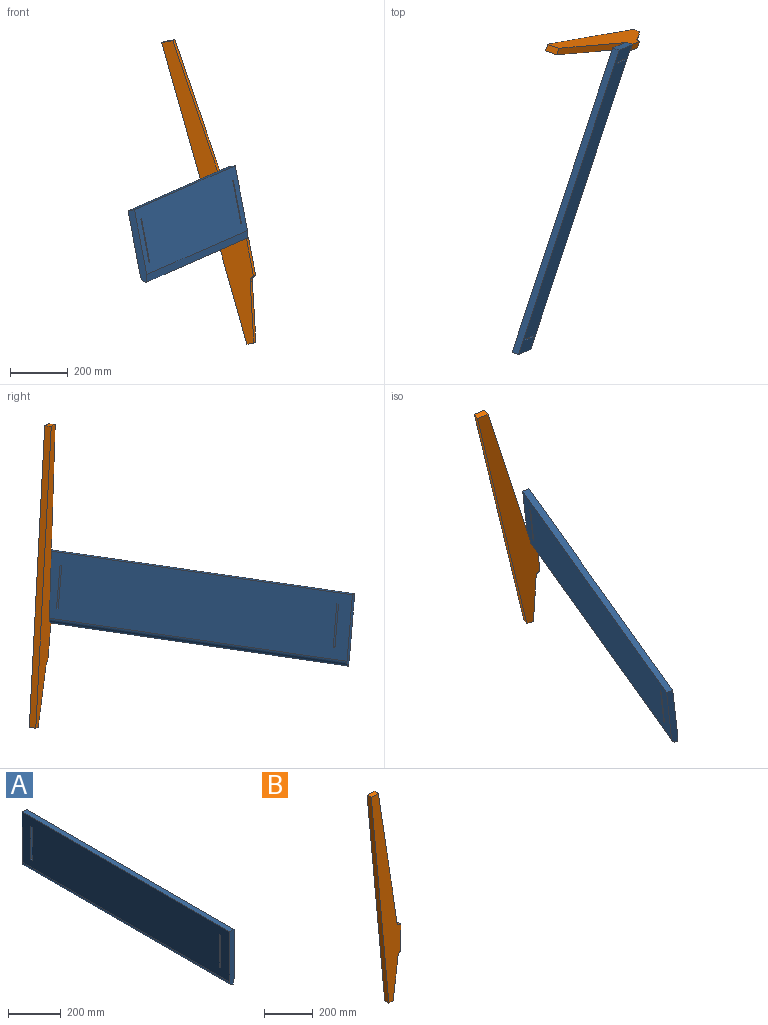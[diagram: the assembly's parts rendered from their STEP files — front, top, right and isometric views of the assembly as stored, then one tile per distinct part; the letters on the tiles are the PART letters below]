
ASSEMBLY  parts=2 mates=1
PART A: 15 faces, bbox 23.8x1117.6x254 mm
  f0: plane 254x23.81mm, normal (0,-1,0), area 5909.4mm2, adj f10,f11,f12,f13,f14
  f1: plane 254x23.81mm, normal (0,1,0), area 5909.4mm2, adj f10,f11,f12,f13,f14
  f2: plane 23.81x6.35mm, normal (0,0,-1), area 151.2mm2, adj f3,f8,f11,f12
  f3: plane 152.4x23.81mm, normal (0,-1,0), area 3629mm2, adj f2,f4,f11,f12
  f4: plane 23.81x6.35mm, normal (0,0,1), area 151.2mm2, adj f3,f8,f11,f12
  f5: plane 23.81x6.35mm, normal (0,0,-1), area 151.2mm2, adj f6,f9,f11,f12
  f6: plane 152.4x23.81mm, normal (0,-1,0), area 3629mm2, adj f5,f7,f11,f12
  f7: plane 23.81x6.35mm, normal (0,0,1), area 151.2mm2, adj f6,f9,f11,f12
  f8: plane 152.4x23.81mm, normal (0,1,0), area 3629mm2, adj f2,f4,f11,f12
  f9: plane 152.4x23.81mm, normal (0,1,0), area 3629mm2, adj f5,f7,f11,f12
  f10: plane 1117.6x23.81mm, normal (0,0,1), area 26612.8mm2, adj f0,f1,f11,f12
  f11: plane 1117.6x228.6mm, normal (1,0,0), area 253547.9mm2, adj f0,f1,f2,f3,f4,f5,f6,f7
  f12: plane 1117.6x234.44mm, normal (-1,0,0), area 260078.3mm2, adj f0,f1,f2,f3,f4,f5,f6,f7
  f13: plane 1117.6x25.4mm, normal (0.98,0,-0.17), area 28825mm2, adj f0,f1,f11,f14
  f14: cylinder r=19.56mm len=1117.6mm, axis (0,1,0), area 34083.9mm2, adj f0,f1,f12,f13
PART B: 10 faces, bbox 171.5x23.8x1079.5 mm
  f0: plane 132.36x23.81mm, normal (1,0,0), area 3151.8mm2, adj f1,f7,f8,f9
  f1: cylinder r=23.64mm len=23.81mm, axis (0,1,0), area 786.3mm2, adj f0,f2,f8,f9
  f2: plane 698.5x107.38mm, normal (0.99,0,0.15), area 16828.4mm2, adj f1,f3,f8,f9
  f3: plane 41.21x23.81mm, normal (0,0,1), area 981.3mm2, adj f2,f4,f8,f9
  f4: plane 1079.5x101.6mm, normal (-1,0,-0.09), area 25819.2mm2, adj f3,f5,f8,f9
  f5: plane 25.4x23.81mm, normal (0,0,-1), area 604.8mm2, adj f4,f6,f8,f9
  f6: plane 210.82x28.37mm, normal (0.99,0,-0.13), area 5065.5mm2, adj f5,f7,f8,f9
  f7: cylinder r=21.18mm len=23.81mm, axis (0,1,0), area 606.7mm2, adj f0,f6,f8,f9
  f8: plane 1079.5x171.45mm, normal (0,-1,0), area 69843.8mm2, adj f0,f1,f2,f3,f4,f5,f6,f7
  f9: plane 1079.5x171.45mm, normal (0,1,0), area 69843.8mm2, adj f0,f1,f2,f3,f4,f5,f6,f7
PLACE A rot(axis=(0.29,-0.44,-0.85),22.2deg) t=(0.87,-545.38,265.85)mm
PLACE B rot(axis=(0.29,-0.44,-0.85),22.2deg) t=(99.65,47.12,-35.81)mm
MATE fastened B.f9 <-> A.f1  axis (0.31,0.94,0.14) through (171.22,-21.41,361.13)mm
